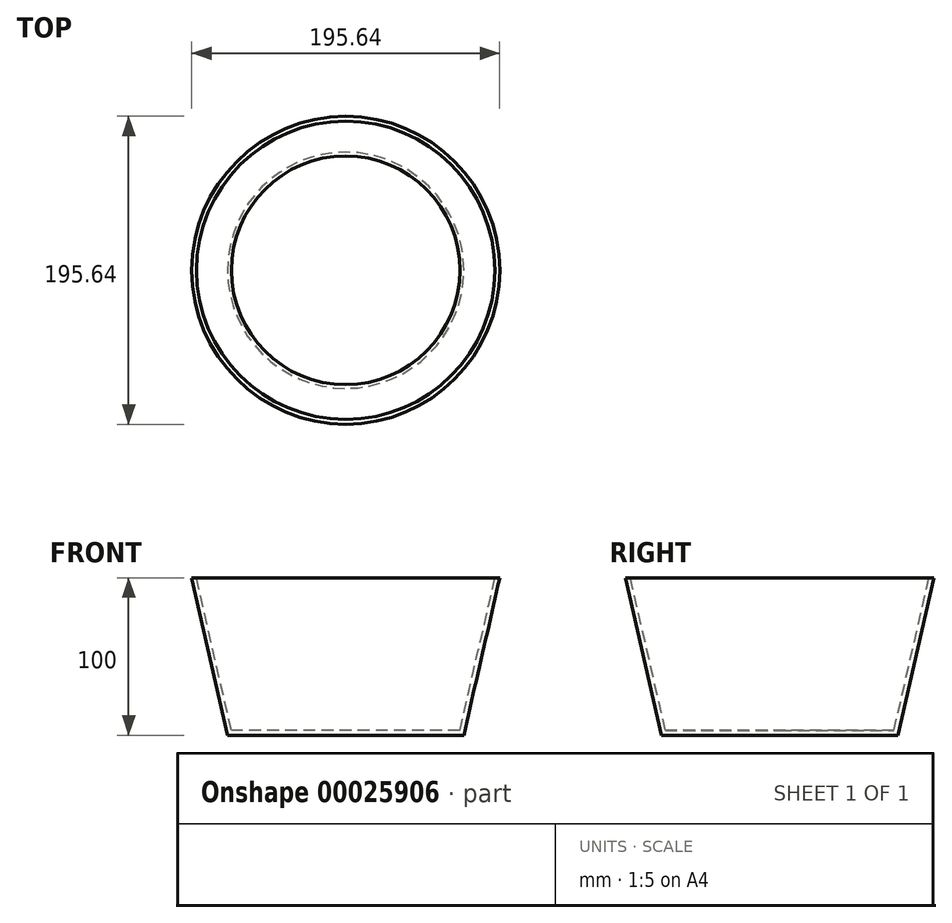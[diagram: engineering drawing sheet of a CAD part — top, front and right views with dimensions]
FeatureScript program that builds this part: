
annotation { "Feature Type Name" : "Feature", "Feature Type Description" : "" }
export const myFeature = defineFeature(function(context is Context, id is Id, definition is map)
    precondition{}
    {
        {
            var Q0;
            Q0=qCreatedBy(makeId("Top.planeOp"),FACE);
            var sketch = newSketch(context, id + "F0", { "sketchPlane" : qUnion([Q0])});
            skCircle(sketch, "E0", {"center": v(0, 0) * mm, "radius": 75 * mm});
            skSolve(sketch);
        }
        {
            var Q0;
            Q0=qCreatedBy(makeId("Top.planeOp"),FACE);
            cPlane(context, id + "F1", {"entities" : qUnion([Q0]), "cplaneType" : CPlaneType.OFFSET, "offset" : 100 * mm, "width" : 150 * mm, "height" : 150 * mm});
        }
        {
            var Q0;
            Q0=qCreatedBy(id+"F1.planeOp",FACE);
            var sketch = newSketch(context, id + "F2", { "sketchPlane" : qUnion([Q0])});
            skCircle(sketch, "E1", {"center": v(0, 0) * mm, "radius": 97.82 * mm});
            skSolve(sketch);
        }
        {
            var Q0;
            Q0=makeQuery(id+"F0.imprint","IMPRINT",FACE,{"disambiguationData":[TD([[makeQuery(id+"F0.imprint","IMPRINT",EDGE,{"derivedFrom":sQuery(id+"F0.wireOp",EDGE,"E0")}),1.0]])]});
            var Q1;
            Q1=makeQuery(id+"F2.imprint","IMPRINT",FACE,{"disambiguationData":[TD([[makeQuery(id+"F2.imprint","IMPRINT",EDGE,{"derivedFrom":sQuery(id+"F2.wireOp",EDGE,"E1")}),1.0]])]});
            loft(context, id + "F3", {"sheetProfilesArray" : [{ "sheetProfileEntities" : qUnion([Q0]) }, { "sheetProfileEntities" : qUnion([Q1]) }]});
        }
        {
            var Q0;
            Q0=makeQuery(id+"F3.opLoft","CAP_FACE",FACE,{"disambiguationData":[OSD([makeQuery(id+"F2.imprint","IMPRINT",FACE,{"disambiguationData":[TD([[makeQuery(id+"F2.imprint","IMPRINT",EDGE,{"derivedFrom":sQuery(id+"F2.wireOp",EDGE,"E1")}),1.0]])]})])],"isStart":true});
            shell(context, id + "F4", {"entities" : qUnion([Q0]), "thickness" : 3 * mm});
        }
    });
